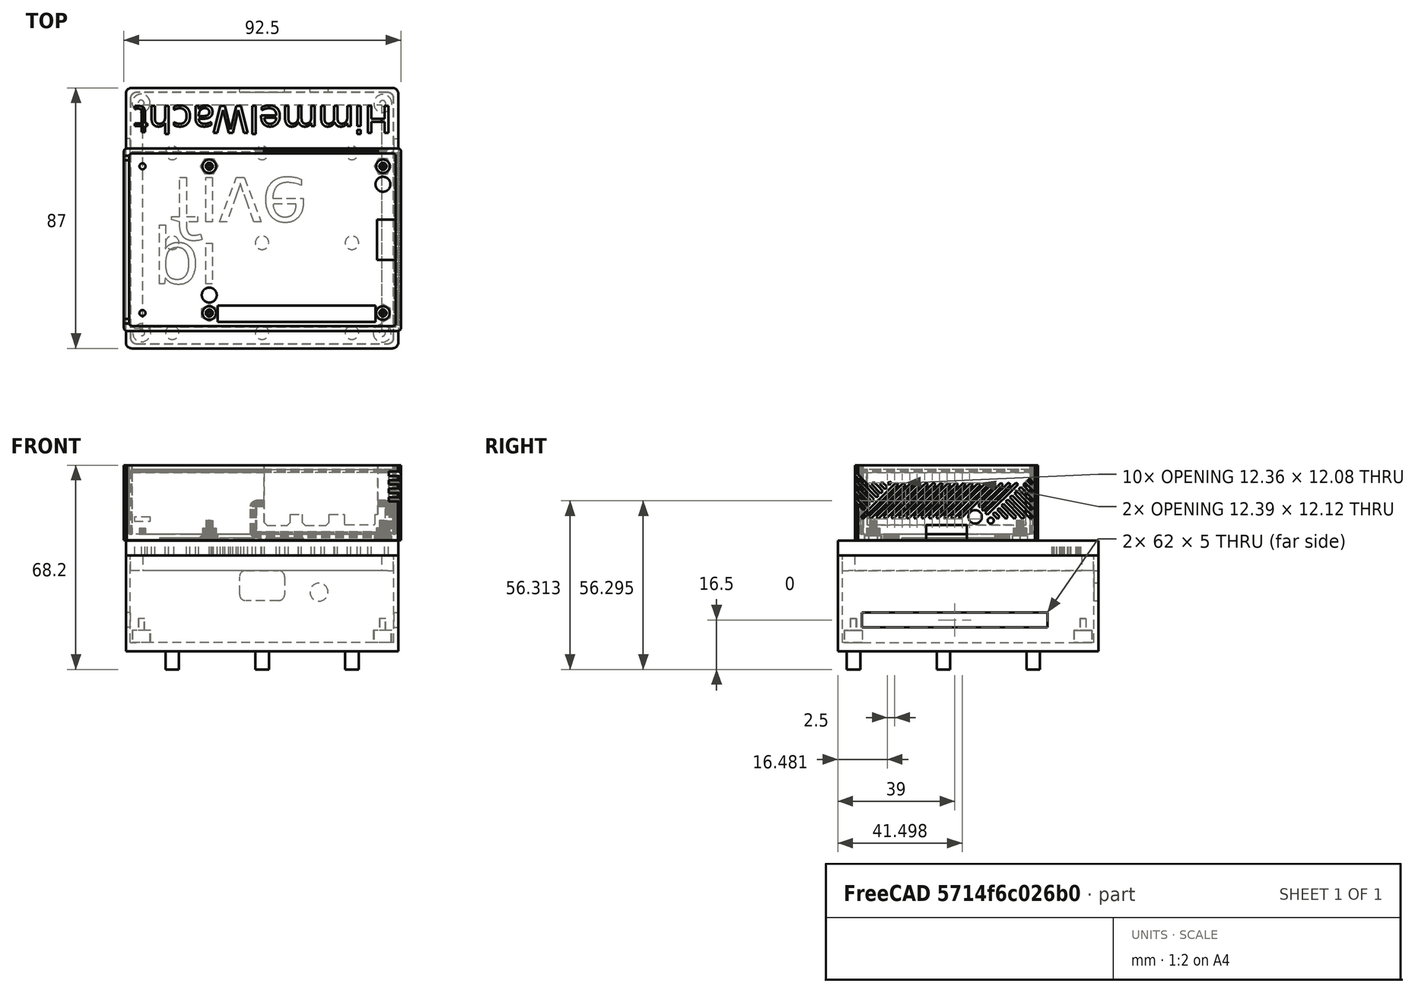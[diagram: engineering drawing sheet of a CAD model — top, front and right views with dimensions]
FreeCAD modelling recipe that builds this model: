
FCSTD DOCUMENT  (FreeCAD 1.0R39109 (Git))
Label: esp-pfusch
License: All rights reserved
LicenseURL: https://en.wikipedia.org/wiki/All_rights_reserved
objects: Part::Fillet×16, Sketcher::SketchObject×14, Part::Extrusion×14, Part::MultiFuse×8, Part::Cut×6, Part::Feature×2, Part::Box×1, Mesh::Feature×1, Part::Refine×1, Part::Part2DObjectPython×1
note: 77 computed .brp shape members not serialized (recipe doc carries the construction recipe); baked Part::Feature solids carry a one-line shape summary decoded from their .brp

FEATURE [Part::Box] Box  label="Cube"
  AttacherType = Attacher::AttachEngine3D
  Height = 3
  Length = 91
  Width = 87
FEATURE [Sketcher::SketchObject] Sketch
  ArcFitTolerance = 1e-06
  AttachmentSupport = -> [Box]
  ExternalGeometry = -> [Box]
  FullyConstrained = true
  MakeInternals = false
  MapMode = 5
  Placement = pos=(0,0,3) rot=(0,0,1;0rad)
  sketch-geometry (4):
    g0: LineSegment StartX=0 StartY=87 StartZ=0 EndX=0 EndY=0 EndZ=0
    g1: LineSegment StartX=0 StartY=0 StartZ=0 EndX=91 EndY=0 EndZ=0
    g2: LineSegment StartX=91 StartY=0 StartZ=0 EndX=91 EndY=87 EndZ=0
    g3: LineSegment StartX=91 StartY=87 StartZ=0 EndX=0 EndY=87 EndZ=0
  constraints (11):
    c: Distance(g-3) = 91
    c: Coincident(g0,g1)
    c: Coincident(g1,g2)
    c: Coincident(g2,g3)
    c: Coincident(g3,g0)
    c: Vertical(g0)
    c: Vertical(g2)
    c: Horizontal(g1)
    c: Horizontal(g3)
    c: Coincident(g0,g-6)
    c: Coincident(g1,g-5)
FEATURE [Sketcher::SketchObject] Sketch001
  ArcFitTolerance = 1e-06
  AttachmentSupport = -> [Box]
  ExternalGeometry = -> [Box]
  FullyConstrained = true
  MakeInternals = false
  MapMode = 5
  Placement = pos=(0,0,3) rot=(0,0,1;0rad)
  sketch-geometry (4):
    g0: LineSegment StartX=1.5 StartY=85.5 StartZ=0 EndX=1.5 EndY=1.5 EndZ=0
    g1: LineSegment StartX=1.5 StartY=1.5 StartZ=0 EndX=89.5 EndY=1.5 EndZ=0
    g2: LineSegment StartX=89.5 StartY=1.5 StartZ=0 EndX=89.5 EndY=85.5 EndZ=0
    g3: LineSegment StartX=89.5 StartY=85.5 StartZ=0 EndX=1.5 EndY=85.5 EndZ=0
  constraints (12):
    c: Coincident(g0,g1)
    c: Coincident(g1,g2)
    c: Coincident(g2,g3)
    c: Coincident(g3,g0)
    c: Vertical(g0)
    c: Vertical(g2)
    c: Horizontal(g1)
    c: Horizontal(g3)
    c: Distance(g0,g-4) = 1.5
    c: Distance(g0,g-3) = 1.5
    c: Distance(g1,g-5) = 1.5
    c: Distance(g1,g-6) = 1.5
FEATURE [Part::Extrusion] Extrude
  Base = -> Sketch
  Dir = (0,0,1)
  DirMode = 2
  FaceMakerClass = Part::FaceMakerBullseye
  FaceMakerMode = 3
  LengthFwd = 29
  LengthRev = 0
  Solid = true
  Symmetric = false
FEATURE [Part::Extrusion] Extrude001
  Base = -> Sketch001
  Dir = (0,0,1)
  DirMode = 2
  FaceMakerClass = Part::FaceMakerBullseye
  FaceMakerMode = 3
  LengthFwd = 29
  LengthRev = 0
  Solid = true
  Symmetric = false
FEATURE [Part::Cut] Cut
  Base = -> Extrude
  Tool = -> Extrude001
FEATURE [Part::MultiFuse] Fusion
  Shapes = -> [Box,Cut]
FEATURE [Part::Fillet] Fillet
  Base = -> Fusion
  EdgeLinks = -> Fusion [Edge3,Edge8]
  Edges = 2 edges r=2: [Edge3,Edge8]
FEATURE [Part::Fillet] Fillet001
  Base = -> Fillet
  EdgeLinks = -> Fillet [Edge30]
  Edges = 1 edges r=2: [Edge30]
FEATURE [Part::Fillet] Fillet002
  Base = -> Fillet001
  EdgeLinks = -> Fillet001 [Edge23]
  Edges = 1 edges r=2: [Edge23]
FEATURE [Part::Fillet] Fillet003
  Base = -> Fillet002
  EdgeLinks = -> Fillet002 [Edge20]
  Edges = 1 edges r=2: [Edge20]
FEATURE [Part::Fillet] Fillet004
  Base = -> Fillet003
  EdgeLinks = -> Fillet003 [Edge21]
  Edges = 1 edges r=2: [Edge21]
FEATURE [Part::Fillet] Fillet005
  Base = -> Fillet004
  EdgeLinks = -> Fillet004 [Edge38]
  Edges = 1 edges r=2: [Edge38]
FEATURE [Part::Fillet] Fillet006
  Base = -> Fillet005
  EdgeLinks = -> Fillet005 [Edge23]
  Edges = 1 edges r=2: [Edge23]
FEATURE [Part::Fillet] Fillet007
  Base = -> Fillet006
  EdgeLinks = -> Fillet006 [Edge24]
  Edges = 1 edges r=2: [Edge24]
FEATURE [Sketcher::SketchObject] Sketch002
  ArcFitTolerance = 1e-06
  AttachmentSupport = -> [Fillet007]
  ExternalGeometry = -> [Fillet007]
  FullyConstrained = true
  MakeInternals = false
  MapMode = 5
  Placement = pos=(0,0,3) rot=(0,0,1;0rad)
  sketch-geometry (4):
    g0: Circle CenterX=5.09336 CenterY=81.8697 CenterZ=0 NormalX=0 NormalY=0 NormalZ=1 AngleXU=0 Radius=3
    g1: Circle CenterX=85.8006 CenterY=81.7832 CenterZ=0 NormalX=0 NormalY=0 NormalZ=1 AngleXU=0 Radius=3
    g2: Circle CenterX=5.27927 CenterY=5.21462 CenterZ=0 NormalX=0 NormalY=0 NormalZ=1 AngleXU=0 Radius=3
    g3: Circle CenterX=85.6315 CenterY=5.09248 CenterZ=0 NormalX=0 NormalY=0 NormalZ=1 AngleXU=0 Radius=3
  constraints (8):
    c: Diameter(g3) = 6
    c: Diameter(g2) = 6
    c: Diameter(g1) = 6
    c: Diameter(g0) = 6
    c: Block(g1)
    c: Block(g0)
    c: Block(g2)
    c: Block(g3)
FEATURE [Part::Extrusion] Extrude002
  Base = -> Sketch002
  Dir = (0,0,1)
  DirMode = 2
  FaceMakerClass = Part::FaceMakerBullseye
  FaceMakerMode = 3
  LengthFwd = 4
  LengthRev = 0
  Solid = true
  Symmetric = false
FEATURE [Part::MultiFuse] Fusion001
  Shapes = -> [Fillet007,Extrude002]
FEATURE [Sketcher::SketchObject] Sketch003
  ArcFitTolerance = 1e-06
  AttachmentSupport = -> [Fusion001]
  ExternalGeometry = -> [Fusion001]
  FullyConstrained = true
  MakeInternals = false
  MapMode = 5
  Placement = pos=(0,0,7) rot=(0,0,1;0rad)
  sketch-geometry (4):
    g0: Circle CenterX=5.3027 CenterY=5.21543 CenterZ=0 NormalX=0 NormalY=0 NormalZ=1 AngleXU=0 Radius=1
    g1: Circle CenterX=85.639 CenterY=5.05661 CenterZ=0 NormalX=0 NormalY=0 NormalZ=1 AngleXU=0 Radius=1
    g2: Circle CenterX=85.7654 CenterY=81.798 CenterZ=0 NormalX=0 NormalY=0 NormalZ=1 AngleXU=0 Radius=1
    g3: Circle CenterX=5.09336 CenterY=81.8697 CenterZ=0 NormalX=0 NormalY=0 NormalZ=1 AngleXU=0 Radius=1
  constraints (9):
    c: Diameter(g0) = 2
    c: Diameter(g1) = 2
    c: Diameter(g2) = 2
    c: Coincident(g3,g-3)
    c: Block(g2)
    c: Block(g3)
    c: Diameter(g3) = 2
    c: Block(g1)
    c: Block(g0)
FEATURE [Part::Extrusion] Extrude003
  Base = -> Sketch003
  Dir = (0,0,1)
  DirMode = 2
  FaceMakerClass = Part::FaceMakerBullseye
  FaceMakerMode = 3
  LengthFwd = 4
  LengthRev = 0
  Solid = true
  Symmetric = false
FEATURE [Part::MultiFuse] Fusion002
  Shapes = -> [Fusion001,Extrude003]
FEATURE [Sketcher::SketchObject] Sketch004
  ArcFitTolerance = 1e-06
  AttachmentSupport = -> [Fusion002]
  ExternalGeometry = -> [Fusion002]
  FullyConstrained = true
  MakeInternals = false
  MapMode = 5
  Placement = pos=(91,0,0) rot=(0.57735,0.57735,0.57735;2.0944rad)
  sketch-geometry (4):
    g0: LineSegment StartX=8 StartY=13 StartZ=0 EndX=8 EndY=8 EndZ=0
    g1: LineSegment StartX=8 StartY=8 StartZ=0 EndX=70 EndY=8 EndZ=0
    g2: LineSegment StartX=70 StartY=8 StartZ=0 EndX=70 EndY=13 EndZ=0
    g3: LineSegment StartX=70 StartY=13 StartZ=0 EndX=8 EndY=13 EndZ=0
  constraints (12):
    c: Coincident(g0,g1)
    c: Coincident(g1,g2)
    c: Coincident(g2,g3)
    c: Coincident(g3,g0)
    c: Vertical(g0)
    c: Vertical(g2)
    c: Horizontal(g1)
    c: Horizontal(g3)
    c: Distance(g0) = 5
    c: Distance(g3) = 62
    c: Distance(g0,g-4) = 5
    c: Distance(g0,g-3) = 6
FEATURE [Part::Extrusion] Extrude004
  Base = -> Sketch004
  Dir = (1,0,0)
  DirMode = 2
  FaceMakerClass = Part::FaceMakerBullseye
  FaceMakerMode = 3
  LengthFwd = 0
  LengthRev = 2
  Solid = true
  Symmetric = false
FEATURE [Part::Cut] Cut001
  Base = -> Fusion002
  Tool = -> Extrude004
FEATURE [Sketcher::SketchObject] Sketch005
  ArcFitTolerance = 1e-06
  AttachmentSupport = -> [Cut001]
  ExternalGeometry = -> [Cut001]
  FullyConstrained = true
  MakeInternals = false
  MapMode = 5
  Placement = pos=(0,0,0) rot=(0.57735,-0.57735,-0.57735;2.0944rad)
  sketch-geometry (4):
    g0: LineSegment StartX=-70 StartY=13 StartZ=0 EndX=-70 EndY=8 EndZ=0
    g1: LineSegment StartX=-70 StartY=8 StartZ=0 EndX=-8 EndY=8 EndZ=0
    g2: LineSegment StartX=-8 StartY=8 StartZ=0 EndX=-8 EndY=13 EndZ=0
    g3: LineSegment StartX=-8 StartY=13 StartZ=0 EndX=-70 EndY=13 EndZ=0
  constraints (12):
    c: Coincident(g0,g1)
    c: Coincident(g1,g2)
    c: Coincident(g2,g3)
    c: Coincident(g3,g0)
    c: Vertical(g0)
    c: Vertical(g2)
    c: Horizontal(g1)
    c: Horizontal(g3)
    c: Distance(g1,g-3) = 6
    c: Distance(g1,g-4) = 5
    c: Distance(g0) = 5
    c: Distance(g3) = 62
FEATURE [Part::Extrusion] Extrude005
  Base = -> Sketch005
  Dir = (-1,0,0)
  DirMode = 2
  FaceMakerClass = Part::FaceMakerBullseye
  FaceMakerMode = 3
  LengthFwd = 0
  LengthRev = 2
  Solid = true
  Symmetric = false
FEATURE [Part::Cut] Cut002
  Base = -> Cut001
  Tool = -> Extrude005
FEATURE [Sketcher::SketchObject] Sketch006
  ArcFitTolerance = 1e-06
  AttachmentSupport = -> [Cut002]
  ExternalGeometry = -> [Cut002]
  FullyConstrained = true
  MakeInternals = false
  MapMode = 5
  Placement = pos=(0,87,0) rot=(0,0.707107,0.707107;3.14159rad)
  sketch-geometry (5):
    g0: LineSegment StartX=-53 StartY=27 StartZ=0 EndX=-53 EndY=17 EndZ=0
    g1: LineSegment StartX=-53 StartY=17 StartZ=0 EndX=-38 EndY=17 EndZ=0
    g2: LineSegment StartX=-38 StartY=17 StartZ=0 EndX=-38 EndY=27 EndZ=0
    g3: LineSegment StartX=-38 StartY=27 StartZ=0 EndX=-53 EndY=27 EndZ=0
    g4: Circle CenterX=-64.5 CenterY=19.8021 CenterZ=0 NormalX=0 NormalY=0 NormalZ=1 AngleXU=0 Radius=3
  constraints (16):
    c: Coincident(g0,g1)
    c: Coincident(g1,g2)
    c: Coincident(g2,g3)
    c: Coincident(g3,g0)
    c: Vertical(g0)
    c: Vertical(g2)
    c: Horizontal(g1)
    c: Horizontal(g3)
    c: Distance(g3) = 15
    c: Distance(g0) = 10
    c: Distance(g-3) = 87
    c: Distance(g2,g-3) = 5
    c: Distance(g2,g-4) = 36
    c: Diameter(g4) = 6
    c: Distance(g4,g0) = 11.5
    c: Block(g4)
FEATURE [Part::Extrusion] Extrude006
  Base = -> Sketch006
  Dir = (0,1,-2e-16)
  DirMode = 2
  FaceMakerClass = Part::FaceMakerBullseye
  FaceMakerMode = 3
  LengthFwd = 0
  LengthRev = 2
  Solid = true
  Symmetric = false
FEATURE [Part::Cut] Cut003
  Base = -> Cut002
  Tool = -> Extrude006
FEATURE [Part::Fillet] Fillet008
  Base = -> Cut003
  EdgeLinks = -> Cut003 [Edge89]
  Edges = 1 edges r=2: [Edge89]
FEATURE [Part::Fillet] Fillet009
  Base = -> Fillet008
  EdgeLinks = -> Fillet008 [Edge16]
  Edges = 1 edges r=2: [Edge16]
FEATURE [Part::Fillet] Fillet010
  Base = -> Fillet009
  EdgeLinks = -> Fillet009 [Edge19]
  Edges = 1 edges r=2: [Edge19]
FEATURE [Part::Fillet] Fillet011
  Base = -> Fillet010
  EdgeLinks = -> Fillet010 [Edge22]
  Edges = 1 edges r=2: [Edge22]
FEATURE [Sketcher::SketchObject] Sketch007
  ArcFitTolerance = 1e-06
  AttachmentSupport = -> [Fillet011]
  ExternalGeometry = -> [Fillet011]
  FullyConstrained = true
  MakeInternals = false
  MapMode = 5
  Placement = pos=(0,0,0) rot=(1,0,0;3.14159rad)
  sketch-geometry (9):
    g0: Circle CenterX=45.5 CenterY=-5.25 CenterZ=0 NormalX=0 NormalY=0 NormalZ=1 AngleXU=0 Radius=2.25
    g1: Circle CenterX=75.5 CenterY=-5.25 CenterZ=0 NormalX=0 NormalY=0 NormalZ=1 AngleXU=0 Radius=2.25
    g2: Circle CenterX=15.5 CenterY=-5.25 CenterZ=0 NormalX=0 NormalY=0 NormalZ=1 AngleXU=0 Radius=2.25
    g3: Circle CenterX=15.5 CenterY=-35.25 CenterZ=0 NormalX=0 NormalY=0 NormalZ=1 AngleXU=0 Radius=2.25
    g4: Circle CenterX=45.5 CenterY=-35.25 CenterZ=0 NormalX=0 NormalY=0 NormalZ=1 AngleXU=0 Radius=2.25
    g5: Circle CenterX=75.5 CenterY=-35.25 CenterZ=0 NormalX=0 NormalY=0 NormalZ=1 AngleXU=0 Radius=2.25
    g6: Circle CenterX=15.5 CenterY=-65.25 CenterZ=0 NormalX=0 NormalY=0 NormalZ=1 AngleXU=0 Radius=2.25
    g7: Circle CenterX=45.5 CenterY=-65.25 CenterZ=0 NormalX=0 NormalY=0 NormalZ=1 AngleXU=0 Radius=2.25
    g8: Circle CenterX=75.5 CenterY=-65.25 CenterZ=0 NormalX=0 NormalY=0 NormalZ=1 AngleXU=0 Radius=2.25
  constraints (27):
    c: Equal(g6,g7)
    c: Equal(g6,g8)
    c: Equal(g6,g5)
    c: Equal(g6,g4)
    c: Equal(g6,g3)
    c: Equal(g6,g0)
    c: Equal(g6,g1)
    c: Diameter(g6) = 4.5
    c: Diameter(g2) = 4.5
    c: Distance(g2,g0) = 30
    c: Distance(g0,g1) = 30
    c: Distance(g0,g4) = 30
    c: Distance(g4,g5) = 30
    c: Distance(g3,g4) = 30
    c: Distance(g4,g7) = 30
    c: Distance(g3,g6) = 30
    c: Distance(g5,g8) = 30
    c: Distance(g0,g-4) = 5.25
    c: Distance(g2,g-4) = 5.25
    c: Distance(g1,g-4) = 5.25
    c: Distance(g3,g2) = 30
    c: Distance(g5,g1) = 30
    c: Distance(g7,g6) = 30
    c: Distance(g7,g8) = 30
    c: Distance(g4,g-5) = 45.5
    c: Distance(g0,g-5) = 45.5
    c: Distance(g7,g-5) = 45.5
FEATURE [Part::Extrusion] Extrude007
  Base = -> Sketch007
  Dir = (0,0,-1)
  DirMode = 2
  FaceMakerClass = Part::FaceMakerBullseye
  FaceMakerMode = 3
  LengthFwd = 6
  LengthRev = 0
  Solid = true
  Symmetric = false
FEATURE [Part::MultiFuse] Fusion003  label="esp-case-bottom"
  Shapes = -> [Fillet011,Extrude007]
FEATURE [Sketcher::SketchObject] Sketch008
  ArcFitTolerance = 1e-06
  AttachmentSupport = -> [Fusion003]
  ExternalGeometry = -> [Fusion003]
  FullyConstrained = true
  MakeInternals = false
  MapMode = 5
  Placement = pos=(0,0,32) rot=(0,0,1;0rad)
  sketch-geometry (8):
    g0: LineSegment StartX=1.201e-13 StartY=2 StartZ=0 EndX=1.197e-13 EndY=85 EndZ=0
    g1: LineSegment StartX=89 StartY=87 StartZ=0 EndX=2 EndY=87 EndZ=0
    g2: LineSegment StartX=91 StartY=85 StartZ=0 EndX=91 EndY=2 EndZ=0
    g3: LineSegment StartX=89 StartY=8.93e-14 StartZ=0 EndX=2 EndY=1.206e-13 EndZ=0
    g4: ArcOfCircle CenterX=2 CenterY=2 CenterZ=0 NormalX=0 NormalY=0 NormalZ=1 AngleXU=0 Radius=2 StartAngle=3.14159 EndAngle=4.71239
    g5: ArcOfCircle CenterX=89 CenterY=2 CenterZ=0 NormalX=0 NormalY=0 NormalZ=1 AngleXU=0 Radius=2 StartAngle=4.71239 EndAngle=6.28319
    g6: ArcOfCircle CenterX=89 CenterY=85 CenterZ=0 NormalX=0 NormalY=0 NormalZ=1 AngleXU=0 Radius=2 StartAngle=0 EndAngle=1.5708
    g7: ArcOfCircle CenterX=2 CenterY=85 CenterZ=0 NormalX=0 NormalY=0 NormalZ=1 AngleXU=0 Radius=2 StartAngle=1.5708 EndAngle=3.14159
  constraints (18):
    c: Coincident(g0,g-9)
    c: Coincident(g0,g-10)
    c: Coincident(g2,g-11)
    c: Coincident(g2,g-6)
    c: Coincident(g4,g-8)
    c: Coincident(g4,g3)
    c: Coincident(g4,g0)
    c: Coincident(g5,g-6)
    c: Coincident(g5,g3)
    c: Coincident(g5,g2)
    c: Coincident(g6,g-11)
    c: Coincident(g6,g2)
    c: Coincident(g6,g1)
    c: Coincident(g7,g-10)
    c: Coincident(g7,g1)
    c: Coincident(g7,g0)
    c: Block(g3)
    c: Block(g1)
FEATURE [Part::Extrusion] Extrude008
  Base = -> Sketch008
  Dir = (0,0,1)
  DirMode = 2
  FaceMakerClass = Part::FaceMakerBullseye
  FaceMakerMode = 3
  LengthFwd = 5
  LengthRev = 0
  Solid = true
  Symmetric = false
FEATURE [Sketcher::SketchObject] Sketch009
  ArcFitTolerance = 1e-06
  AttachmentSupport = -> [Fusion003]
  ExternalGeometry = -> [Fusion003]
  FullyConstrained = true
  MakeInternals = false
  MapMode = 5
  Placement = pos=(0,0,32) rot=(0,0,1;0rad)
FEATURE [Mesh::Feature] esp_case_pi5_case_bottom  label="esp-case-pi5-case-bottom"
  Placement = pos=(0,116.1,0) rot=(0,0,1;0rad)
FEATURE [Part::Feature] esp_case_pi5_case_bottom001
  shape: large baked B-rep (32 MB .brp); summary skipped
FEATURE [Part::Refine] esp_case_pi5_case_bottom002
  Source = -> esp_case_pi5_case_bottom001
FEATURE [Part::Feature] esp_case_pi5_case_bottom002_solid  label="esp_case_pi5_case_bottom002 (Solid)"
  Placement = pos=(-64.4,-188.4,37.2) rot=(0,0,1;0rad)
  shape: bbox 92.5 x 61 x 25 mm, 20844 faces (baked)
FEATURE [Part::MultiFuse] Fusion004
  Shapes = -> [Extrude008,esp_case_pi5_case_bottom002_solid]
FEATURE [Sketcher::SketchObject] Sketch010
  ArcFitTolerance = 1e-06
  AttachmentSupport = -> [Fusion004]
  FullyConstrained = true
  MakeInternals = false
  MapMode = 5
  Placement = pos=(0,0,38.55) rot=(0,0,1;0rad)
  sketch-geometry (4):
    g0: LineSegment StartX=4.3415 StartY=22.8104 StartZ=0 EndX=82.5521 EndY=22.8104 EndZ=0
    g1: LineSegment StartX=82.5521 StartY=22.8104 StartZ=0 EndX=82.5521 EndY=64.0195 EndZ=0
    g2: LineSegment StartX=82.5521 StartY=64.0195 StartZ=0 EndX=4.3415 EndY=64.0195 EndZ=0
    g3: LineSegment StartX=4.3415 StartY=64.0195 StartZ=0 EndX=4.3415 EndY=22.8104 EndZ=0
  constraints (10):
    c: Coincident(g0,g1)
    c: Coincident(g1,g2)
    c: Coincident(g2,g3)
    c: Coincident(g3,g0)
    c: Horizontal(g0)
    c: Horizontal(g2)
    c: Vertical(g1)
    c: Vertical(g3)
    c: Block(g0)
    c: Block(g3)
FEATURE [Part::Extrusion] Extrude009
  Base = -> Sketch010
  Dir = (0,0,1)
  DirMode = 2
  FaceMakerClass = Part::FaceMakerBullseye
  FaceMakerMode = 3
  LengthFwd = 0.65
  LengthRev = 0
  Solid = true
  Symmetric = false
FEATURE [Sketcher::SketchObject] Sketch011
  ArcFitTolerance = 1e-06
  AttachmentSupport = -> [Fusion004]
  FullyConstrained = true
  MakeInternals = false
  MapMode = 5
  Placement = pos=(0,0,38.55) rot=(0,0,1;0rad)
  sketch-geometry (4):
    g0: LineSegment StartX=81.5781 StartY=14.8464 StartZ=0 EndX=81.5781 EndY=23.2533 EndZ=0
    g1: LineSegment StartX=81.5781 StartY=23.2533 StartZ=0 EndX=58.1692 EndY=23.2533 EndZ=0
    g2: LineSegment StartX=58.1692 StartY=23.2533 StartZ=0 EndX=58.1692 EndY=14.8464 EndZ=0
    g3: LineSegment StartX=58.1692 StartY=14.8464 StartZ=0 EndX=81.5781 EndY=14.8464 EndZ=0
  constraints (10):
    c: Coincident(g0,g1)
    c: Coincident(g1,g2)
    c: Coincident(g2,g3)
    c: Coincident(g3,g0)
    c: Vertical(g0)
    c: Vertical(g2)
    c: Horizontal(g1)
    c: Horizontal(g3)
    c: Block(g1)
    c: Block(g0)
FEATURE [Part::Extrusion] Extrude010
  Base = -> Sketch011
  Dir = (0,0,1)
  DirMode = 2
  FaceMakerClass = Part::FaceMakerBullseye
  FaceMakerMode = 3
  LengthFwd = 0.65
  LengthRev = 0
  Solid = true
  Symmetric = false
FEATURE [Part::MultiFuse] Fusion005
  Shapes = -> [Extrude009,Extrude010]
FEATURE [Part::MultiFuse] Fusion006
  Shapes = -> [Fusion005,Fusion004]
FEATURE [Part::Part2DObjectPython] ShapeString  # Draft 2D object (typed FeaturePython)
  FontFile = <path>
  Fuse = false
  Justification = 6
  JustificationReference = 0
  KeepLeftMargin = false
  MakeFace = true
  ObliqueAngle = 0
  Placement = pos=(273.43,28.24,0) rot=(0,0,1;0rad)
  ScaleToSize = true
  Size = 9
  String = HimmelWacht
  Tracking = 0
FEATURE [Part::Extrusion] Extrude011
  Base = -> ShapeString
  Dir = (0,0,1)
  DirMode = 2
  FaceMakerClass = Part::FaceMakerBullseye
  FaceMakerMode = 3
  LengthFwd = 10
  LengthRev = 0
  Placement = pos=(361.1,109.2,31.7) rot=(0,0,-1;3.14159rad)
  Solid = false
  Symmetric = false
FEATURE [Part::Cut] Cut004
  Base = -> Fusion006
  Tool = -> Extrude011
FEATURE [Sketcher::SketchObject] Sketch012
  ArcFitTolerance = 1e-06
  AttachmentSupport = -> [Fusion003]
  ExternalGeometry = -> [Fusion003]
  FullyConstrained = true
  MakeInternals = false
  MapMode = 5
  Placement = pos=(0,0,32) rot=(0,0,1;0rad)
  sketch-geometry (4):
    g0: LineSegment StartX=1.6 StartY=1.6 StartZ=0 EndX=89.4 EndY=1.6 EndZ=0
    g1: LineSegment StartX=89.4 StartY=1.6 StartZ=0 EndX=89.4 EndY=85.4 EndZ=0
    g2: LineSegment StartX=89.4 StartY=85.4 StartZ=0 EndX=1.6 EndY=85.4 EndZ=0
    g3: LineSegment StartX=1.6 StartY=85.4 StartZ=0 EndX=1.6 EndY=1.6 EndZ=0
  constraints (12):
    c: Coincident(g0,g1)
    c: Coincident(g1,g2)
    c: Coincident(g2,g3)
    c: Coincident(g3,g0)
    c: Horizontal(g0)
    c: Horizontal(g2)
    c: Vertical(g1)
    c: Vertical(g3)
    c: Distance(g0,g-2) = 1.6
    c: Distance(g0,g-1) = 1.6
    c: Distance(g1,g-7) = 1.6
    c: Distance(g1,g-9) = 1.6
FEATURE [Part::Extrusion] Extrude012
  Base = -> Sketch012
  Dir = (0,0,1)
  DirMode = 2
  FaceMakerClass = Part::FaceMakerBullseye
  FaceMakerMode = 3
  LengthFwd = 0
  LengthRev = 5
  Solid = true
  Symmetric = false
FEATURE [Sketcher::SketchObject] Sketch013
  ArcFitTolerance = 1e-06
  AttachmentSupport = -> [Extrude012]
  ExternalGeometry = -> [Extrude012]
  FullyConstrained = true
  MakeInternals = false
  MapMode = 5
  Placement = pos=(0,0,27) rot=(1,0,0;3.14159rad)
  sketch-geometry (4):
    g0: LineSegment StartX=5.6 StartY=-5.6 StartZ=0 EndX=5.6 EndY=-81.4 EndZ=0
    g1: LineSegment StartX=5.6 StartY=-81.4 StartZ=0 EndX=85.4 EndY=-81.4 EndZ=0
    g2: LineSegment StartX=85.4 StartY=-81.4 StartZ=0 EndX=85.4 EndY=-5.6 EndZ=0
    g3: LineSegment StartX=85.4 StartY=-5.6 StartZ=0 EndX=5.6 EndY=-5.6 EndZ=0
  constraints (12):
    c: Coincident(g0,g1)
    c: Coincident(g1,g2)
    c: Coincident(g2,g3)
    c: Coincident(g3,g0)
    c: Vertical(g0)
    c: Vertical(g2)
    c: Horizontal(g1)
    c: Horizontal(g3)
    c: Distance(g0,g-3) = 4
    c: Distance(g0,g-5) = 4
    c: Distance(g1,g-6) = 4
    c: Distance(g1,g-4) = 4
FEATURE [Part::Extrusion] Extrude013
  Base = -> Sketch013
  Dir = (0,0,-1)
  DirMode = 2
  FaceMakerClass = Part::FaceMakerBullseye
  FaceMakerMode = 3
  LengthFwd = 0
  LengthRev = 10
  Solid = true
  Symmetric = false
FEATURE [Part::Cut] Cut005
  Base = -> Extrude012
  Tool = -> Extrude013
FEATURE [Part::Fillet] Fillet012
  Base = -> Cut005
  EdgeLinks = -> Cut005 [Edge1]
  Edges = 1 edges r=2: [Edge1]
FEATURE [Part::Fillet] Fillet013
  Base = -> Fillet012
  EdgeLinks = -> Fillet012 [Edge3]
  Edges = 1 edges r=2: [Edge3]
FEATURE [Part::Fillet] Fillet014
  Base = -> Fillet013
  EdgeLinks = -> Fillet013 [Edge25]
  Edges = 1 edges r=2: [Edge25]
FEATURE [Part::Fillet] Fillet015
  Base = -> Fillet014
  EdgeLinks = -> Fillet014 [Edge19]
  Edges = 1 edges r=2: [Edge19]
FEATURE [Part::MultiFuse] Fusion007  label="esp-case-top"
  Shapes = -> [Cut004,Fillet015]
note: 1 file-system path scrubbed to <path> (originals preserved in the JSON sidecar)
